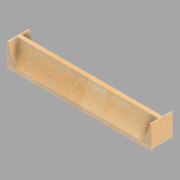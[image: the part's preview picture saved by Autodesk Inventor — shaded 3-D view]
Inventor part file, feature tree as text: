
AUTODESK INVENTOR PART (.ipt)
format: ipt  version: 2022.2 (Build 262287010, 287A)  size: 165,888 bytes
history: native  units: in
note: dims shown in document units (in); Inventor stores cm internally (conversion verified against a paired STEP export)
features: plane x1, extrude x1, sketch x1, other x1
ambient origin geometry x8: Origin, YZ Plane, XZ Plane, XY Plane, X Axis, Y Axis, Z Axis, Center Point
bodies: Solid1 (feature_tree)
feature tree (4):
  plane  "Work Plane1"
  extrude  "Extrusion1"  Depth=8.75in
  sketch  "Sketch1"  dims[d0=8.75in d1=8.75in d2=34.875in d3=0.0in]
  other  "North (6) (2) (1)"
